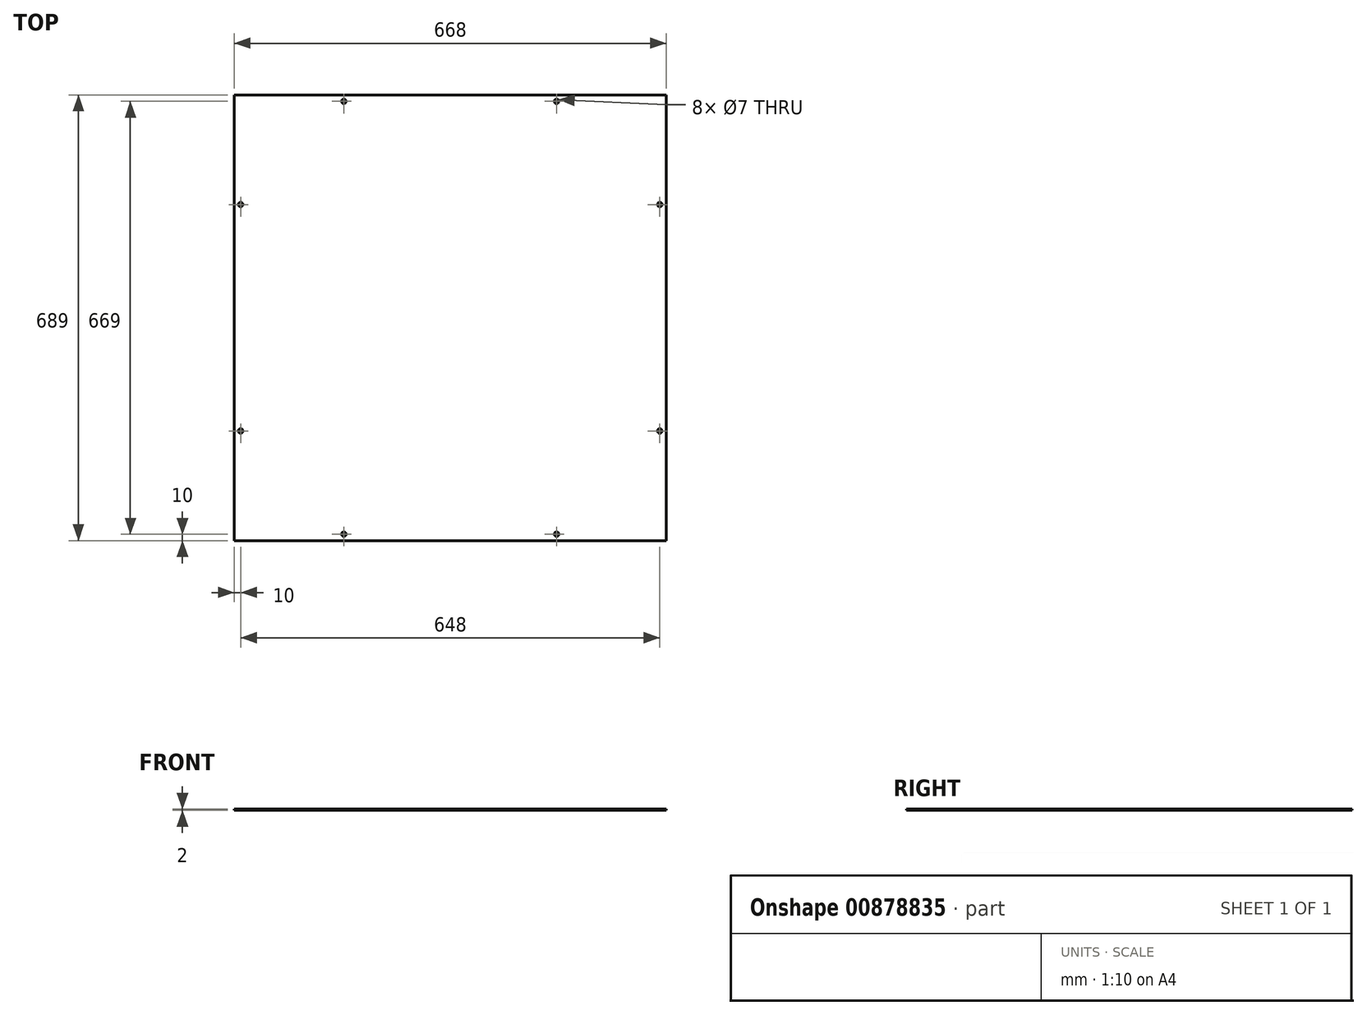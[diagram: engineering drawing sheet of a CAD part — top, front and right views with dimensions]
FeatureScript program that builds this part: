
annotation { "Feature Type Name" : "Feature", "Feature Type Description" : "" }
export const myFeature = defineFeature(function(context is Context, id is Id, definition is map)
    precondition{}
    {
        {
            var Q0;
            Q0=qCreatedBy(makeId("Top.planeOp"),FACE);
            var sketch = newSketch(context, id + "F0", { "sketchPlane" : qUnion([Q0])});
            skLineSegment(sketch, "E0.bottom", {"start": v(0, 0) * mm, "end": v(668, 0) * mm});
            skLineSegment(sketch, "E0.top", {"start": v(0, 689) * mm, "end": v(668, 689) * mm});
            skLineSegment(sketch, "E0.left", {"start": v(0, 0) * mm, "end": v(0, 689) * mm});
            skLineSegment(sketch, "E0.right", {"start": v(668, 0) * mm, "end": v(668, 689) * mm});
            skSolve(sketch);
        }
        {
            var Q0;
            Q0 = qSketchRegion(id + "F0", true);
            extrude(context, id + "F1", {"entities" : qUnion([Q0]), "depth" : 2 * mm, "offsetDistance" : 25 * mm});
        }
        {
            var Q0;
            Q0=makeQuery(id+"F1.opExtrude","CAP_FACE",FACE,{"disambiguationData":[OSD([sQuery(id+"F0.wireOp",EDGE,"E0.bottom"),sQuery(id+"F0.wireOp",EDGE,"E0.top"),sQuery(id+"F0.wireOp",EDGE,"E0.left"),sQuery(id+"F0.wireOp",EDGE,"E0.right")])],"isStart":false});
            var sketch = newSketch(context, id + "F2", { "sketchPlane" : qUnion([Q0])});
            skLineSegment(sketch, "E1", {"start": v(334, 0) * mm, "end": v(334, 689) * mm, "construction": true});
            skLineSegment(sketch, "E2", {"start": v(0, 344.5) * mm, "end": v(668, 344.5) * mm, "construction": true});
            skLineSegment(sketch, "E3", {"start": v(0, 519.5) * mm, "end": v(668, 519.5) * mm, "construction": true});
            skLineSegment(sketch, "E4", {"start": v(0, 169.5) * mm, "end": v(668, 169.5) * mm, "construction": true});
            skLineSegment(sketch, "E5", {"start": v(169.5, 689) * mm, "end": v(169.5, 0) * mm, "construction": true});
            skLineSegment(sketch, "E6.MirrorCS", {"start": v(498.5, 689) * mm, "end": v(498.5, 0) * mm, "construction": true});
            skLineSegment(sketch, "E7", {"start": v(10, 0) * mm, "end": v(10, 689) * mm, "construction": true});
            skLineSegment(sketch, "E8", {"start": v(0, 679) * mm, "end": v(668, 679) * mm, "construction": true});
            skLineSegment(sketch, "E9.MirrorCS", {"start": v(658, 0) * mm, "end": v(658, 689) * mm, "construction": true});
            skLineSegment(sketch, "E10.MirrorCS", {"start": v(0, 10) * mm, "end": v(668, 10) * mm, "construction": true});
            skCircle(sketch, "E11", {"center": v(10, 519.5) * mm, "radius": 3.5 * mm});
            skCircle(sketch, "E12", {"center": v(169.5, 679) * mm, "radius": 3.5 * mm});
            skCircle(sketch, "E13.MirrorC", {"center": v(658, 519.5) * mm, "radius": 3.5 * mm});
            skCircle(sketch, "E14.MirrorC", {"center": v(498.5, 679) * mm, "radius": 3.5 * mm});
            skCircle(sketch, "E15.MirrorC", {"center": v(10, 169.5) * mm, "radius": 3.5 * mm});
            skCircle(sketch, "E16.MirrorC", {"center": v(169.5, 10) * mm, "radius": 3.5 * mm});
            skCircle(sketch, "E17.MirrorC", {"center": v(498.5, 10) * mm, "radius": 3.5 * mm});
            skCircle(sketch, "E18.MirrorC", {"center": v(658, 169.5) * mm, "radius": 3.5 * mm});
            skSolve(sketch);
        }
        {
            var Q0;
            Q0=sQuery(id+"F2.wireOp",VERTEX,"E11.center");
            var Q1;
            Q1=sQuery(id+"F2.wireOp",VERTEX,"E12.center");
            var Q2;
            Q2=sQuery(id+"F2.wireOp",VERTEX,"E14.MirrorC.center");
            var Q3;
            Q3=sQuery(id+"F2.wireOp",VERTEX,"E13.MirrorC.center");
            var Q4;
            Q4=sQuery(id+"F2.wireOp",VERTEX,"E18.MirrorC.center");
            var Q5;
            Q5=sQuery(id+"F2.wireOp",VERTEX,"E17.MirrorC.center");
            var Q6;
            Q6=sQuery(id+"F2.wireOp",VERTEX,"E16.MirrorC.center");
            var Q7;
            Q7=sQuery(id+"F2.wireOp",VERTEX,"E15.MirrorC.center");
            var Q8;
            Q8=makeQuery(id+"F1.opExtrude","SWEPT_BODY",BODY,{"disambiguationData":[OSD([sQuery(id+"F0.wireOp",EDGE,"E0.bottom"),sQuery(id+"F0.wireOp",EDGE,"E0.top"),sQuery(id+"F0.wireOp",EDGE,"E0.left"),sQuery(id+"F0.wireOp",EDGE,"E0.right")])]});
            hole(context, id + "F3", {"style" : HoleStyle.SIMPLE, "endStyle" : HoleEndStyle.THROUGH, "holeDiameter" : 7 * mm, "majorDiameter" : 5 * mm, "isTappedThrough" : true, "tappedDepth" : 12 * mm, "tapClearance" : 3, "locations" : qUnion([Q0, Q1, Q2, Q3, Q4, Q5, Q6, Q7]), "scope" : qUnion([Q8])});
        }
    });
